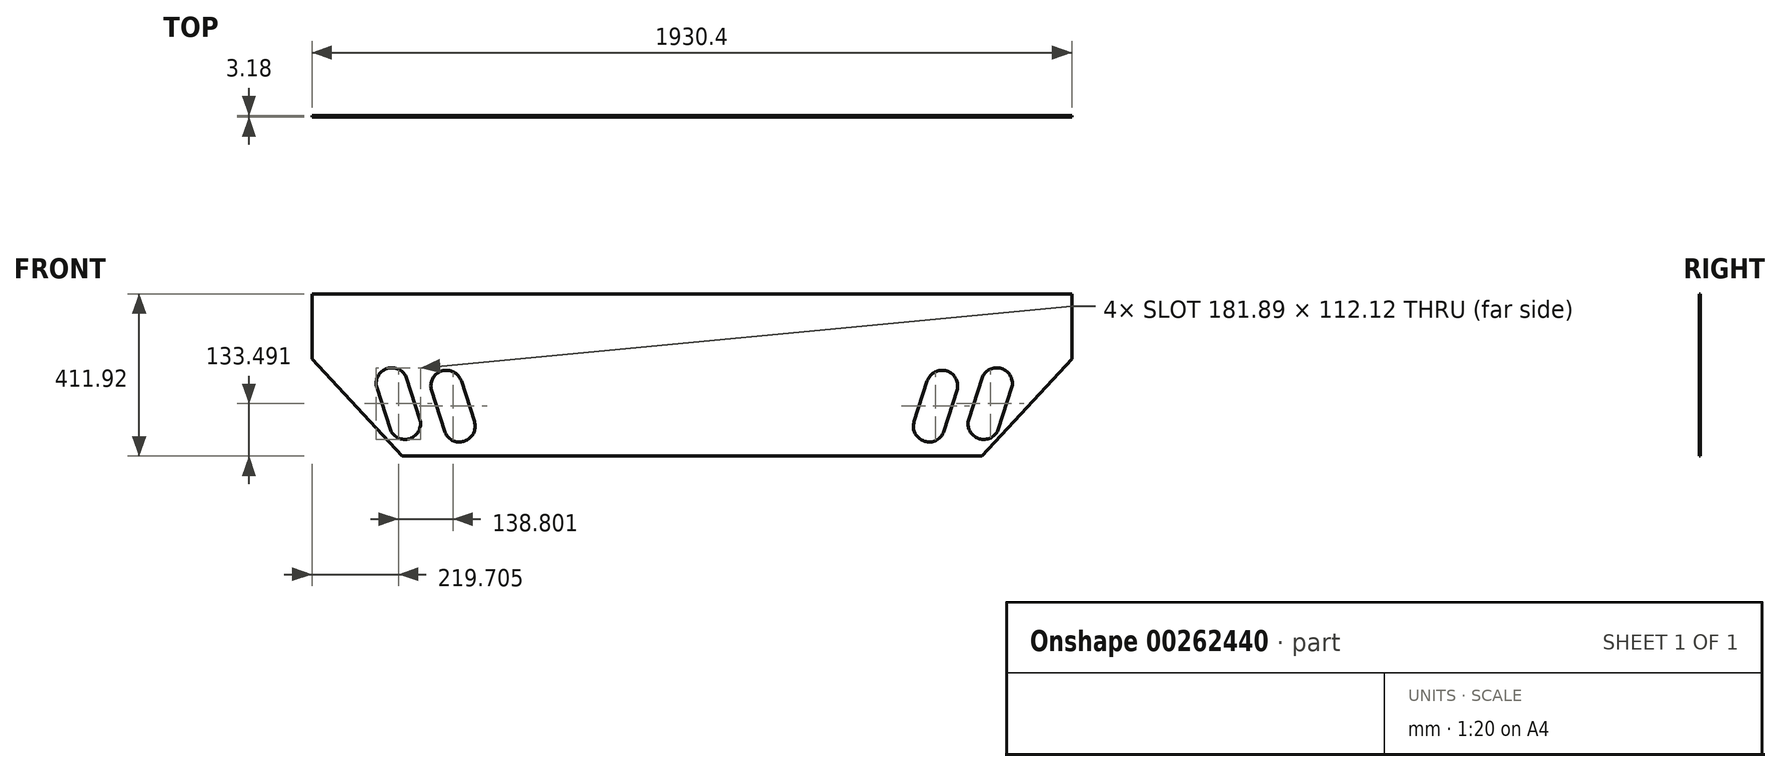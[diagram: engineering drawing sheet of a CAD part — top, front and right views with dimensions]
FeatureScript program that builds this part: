
annotation { "Feature Type Name" : "Feature", "Feature Type Description" : "" }
export const myFeature = defineFeature(function(context is Context, id is Id, definition is map)
    precondition{}
    {
        {
            var Q0;
            Q0=qCreatedBy(makeId("Front.planeOp"),FACE);
            var sketch = newSketch(context, id + "F0", { "sketchPlane" : qUnion([Q0])});
            skLineSegment(sketch, "E0.top", {"start": v(526.84, -123.41) * mm, "end": v(-539.96, -123.41) * mm});
            skPoint(sketch, "E0.middle", {"position": v(0, 0) * mm});
            skLineSegment(sketch, "E1", {"start": v(-539.96, -123.41) * mm, "end": v(526.84, -123.41) * mm});
            skPoint(sketch, "E2.orphan", {"position": v(-958.64, -123.41) * mm});
            skPoint(sketch, "E3.orphan", {"position": v(971.76, -123.41) * mm});
            skLineSegment(sketch, "E4.top", {"start": v(-971.76, 288.51) * mm, "end": v(958.64, 288.51) * mm});
            skLineSegment(sketch, "E4.left", {"start": v(-971.76, 123.41) * mm, "end": v(-971.76, 288.51) * mm});
            skLineSegment(sketch, "E4.right", {"start": v(958.64, 123.41) * mm, "end": v(958.64, 288.51) * mm});
            skLineSegment(sketch, "E5", {"start": v(-539.96, -123.41) * mm, "end": v(-743.16, -123.41) * mm});
            skLineSegment(sketch, "E6", {"start": v(-971.76, 123.41) * mm, "end": v(-743.16, -123.41) * mm});
            skLineSegment(sketch, "E7", {"start": v(730.04, -123.41) * mm, "end": v(958.64, 123.41) * mm});
            skLineSegment(sketch, "E8", {"start": v(526.84, -123.41) * mm, "end": v(730.04, -123.41) * mm});
            skSolve(sketch);
        }
        {
            var Q0;
            Q0 = qSketchRegion(id + "F0", true);
            extrude(context, id + "F1", {"entities" : qUnion([Q0]), "depth" : 3.17 * mm});
        }
        {
            var Q0;
            Q0=makeQuery(id+"F1.opExtrude","CAP_FACE",FACE,{"disambiguationData":[OSD([sQuery(id+"F0.wireOp",EDGE,"E1"),sQuery(id+"F0.wireOp",EDGE,"E4.top"),sQuery(id+"F0.wireOp",EDGE,"E4.left"),sQuery(id+"F0.wireOp",EDGE,"E4.right"),sQuery(id+"F0.wireOp",EDGE,"E5"),sQuery(id+"F0.wireOp",EDGE,"E6"),sQuery(id+"F0.wireOp",EDGE,"E7"),sQuery(id+"F0.wireOp",EDGE,"E8")])],"isStart":false});
            var sketch = newSketch(context, id + "F2", { "sketchPlane" : qUnion([Q0])});
            skLineSegment(sketch, "E9", {"start": v(-768.56, 61.47) * mm, "end": v(-735.55, -41.3) * mm});
            skArc(sketch, "E10.0.startCap", {"start": v(-806.35, 49.34) * mm, "mid": v(-780.7, 99.26) * mm, "end": v(-730.77, 73.6) * mm});
            skArc(sketch, "E10.0.endCap", {"start": v(-697.76, -29.17) * mm, "mid": v(-723.42, -79.1) * mm, "end": v(-773.34, -53.44) * mm});
            skLineSegment(sketch, "E10.0.left", {"start": v(-730.77, 73.6) * mm, "end": v(-697.76, -29.17) * mm});
            skLineSegment(sketch, "E10.0.right", {"start": v(-806.35, 49.34) * mm, "end": v(-773.34, -53.44) * mm});
            skPoint(sketch, "E11.end.orphan", {"position": v(0, 301.24) * mm});
            skPoint(sketch, "E11.start.orphan", {"position": v(0, -123.41) * mm});
            skLineSegment(sketch, "E12", {"start": v(-629.76, 55) * mm, "end": v(-596.75, -47.78) * mm});
            skArc(sketch, "E13.0.startCap", {"start": v(-667.54, 42.87) * mm, "mid": v(-641.9, 92.79) * mm, "end": v(-591.97, 67.14) * mm});
            skArc(sketch, "E13.0.endCap", {"start": v(-558.96, -35.64) * mm, "mid": v(-584.61, -85.56) * mm, "end": v(-634.54, -59.91) * mm});
            skLineSegment(sketch, "E13.0.left", {"start": v(-591.97, 67.14) * mm, "end": v(-558.96, -35.64) * mm});
            skLineSegment(sketch, "E13.0.right", {"start": v(-667.54, 42.87) * mm, "end": v(-634.54, -59.91) * mm});
            skLineSegment(sketch, "E14", {"start": v(-0.2, 288.51) * mm, "end": v(-0.2, -123.41) * mm});
            skArc(sketch, "E15.MirrorCS", {"start": v(667.13, 42.87) * mm, "mid": v(641.48, 92.79) * mm, "end": v(591.56, 67.14) * mm});
            skArc(sketch, "E16.MirrorCS", {"start": v(805.93, 49.34) * mm, "mid": v(780.28, 99.26) * mm, "end": v(730.36, 73.6) * mm});
            skLineSegment(sketch, "E17.MirrorCS", {"start": v(730.36, 73.6) * mm, "end": v(697.35, -29.17) * mm});
            skLineSegment(sketch, "E18.MirrorCS", {"start": v(805.93, 49.34) * mm, "end": v(772.93, -53.44) * mm});
            skArc(sketch, "E19.MirrorCS", {"start": v(697.35, -29.17) * mm, "mid": v(723, -79.1) * mm, "end": v(772.93, -53.44) * mm});
            skLineSegment(sketch, "E20.MirrorCS", {"start": v(667.13, 42.87) * mm, "end": v(634.13, -59.91) * mm});
            skLineSegment(sketch, "E21.MirrorCS", {"start": v(591.56, 67.14) * mm, "end": v(558.55, -35.64) * mm});
            skArc(sketch, "E22.MirrorCS", {"start": v(558.55, -35.64) * mm, "mid": v(584.2, -85.56) * mm, "end": v(634.13, -59.91) * mm});
            skSolve(sketch);
        }
        {
            var Q0;
            Q0 = qSketchRegion(id + "F2", true);
            extrude(context, id + "F3", {"entities" : qUnion([Q0]), "operationType" : NewBodyOperationType.REMOVE, "oppositeDirection" : true, "depth" : 25.4 * mm});
        }
    });
